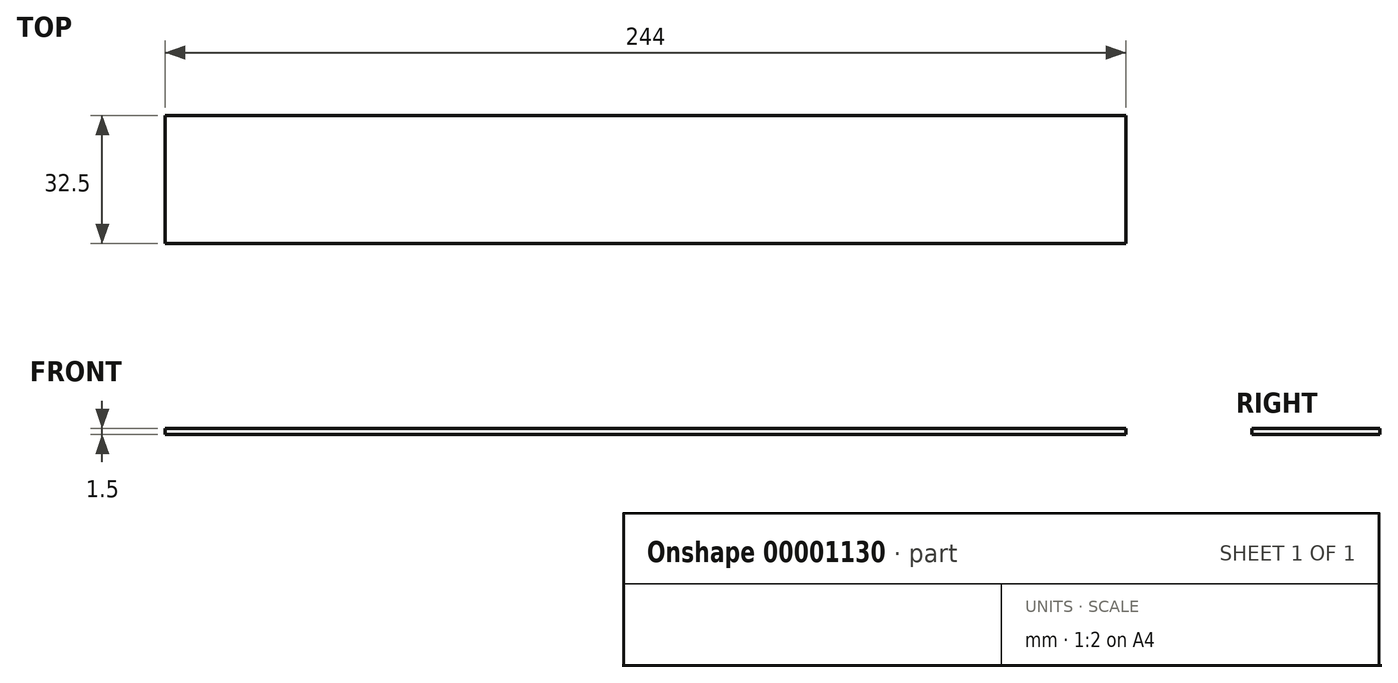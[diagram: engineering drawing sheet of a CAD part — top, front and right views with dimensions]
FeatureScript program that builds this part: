
annotation { "Feature Type Name" : "Feature", "Feature Type Description" : "" }
export const myFeature = defineFeature(function(context is Context, id is Id, definition is map)
    precondition{}
    {
        {
            var Q0;
            Q0=qCreatedBy(makeId("Top.planeOp"),FACE);
            var sketch = newSketch(context, id + "F0", { "sketchPlane" : qUnion([Q0])});
            skLineSegment(sketch, "E0.bottom", {"start": v(0, 0) * mm, "end": v(244, 0) * mm});
            skLineSegment(sketch, "E0.top", {"start": v(0, 32.5) * mm, "end": v(244, 32.5) * mm});
            skLineSegment(sketch, "E0.left", {"start": v(0, 0) * mm, "end": v(0, 32.5) * mm});
            skLineSegment(sketch, "E0.right", {"start": v(244, 0) * mm, "end": v(244, 32.5) * mm});
            skLineSegment(sketch, "E1", {"start": v(22, 0) * mm, "end": v(22, 32.5) * mm, "construction": true});
            skLineSegment(sketch, "E2", {"start": v(78, 0) * mm, "end": v(78, 32.5) * mm, "construction": true});
            skLineSegment(sketch, "E3", {"start": v(130, 0) * mm, "end": v(130, 32.5) * mm, "construction": true});
            skLineSegment(sketch, "E4", {"start": v(176, 0) * mm, "end": v(176, 32.5) * mm, "construction": true});
            skLineSegment(sketch, "E5", {"start": v(222, 0) * mm, "end": v(222, 32.5) * mm, "construction": true});
            skLineSegment(sketch, "E6", {"start": v(0, 6.5) * mm, "end": v(244, 6.5) * mm, "construction": true});
            skLineSegment(sketch, "E7", {"start": v(0, 15.5) * mm, "end": v(244, 15.5) * mm, "construction": true});
            skSolve(sketch);
        }
        {
            var Q0;
            Q0=makeQuery(id+"F0.imprint","IMPRINT",FACE,{"disambiguationData":[TD([[makeQuery(id+"F0.imprint","IMPRINT",EDGE,{"derivedFrom":sQuery(id+"F0.wireOp",EDGE,"E0.bottom")}),1.0]])]});
            extrude(context, id + "F1", {"entities" : qUnion([Q0]), "depth" : 1.5 * mm});
        }
    });
